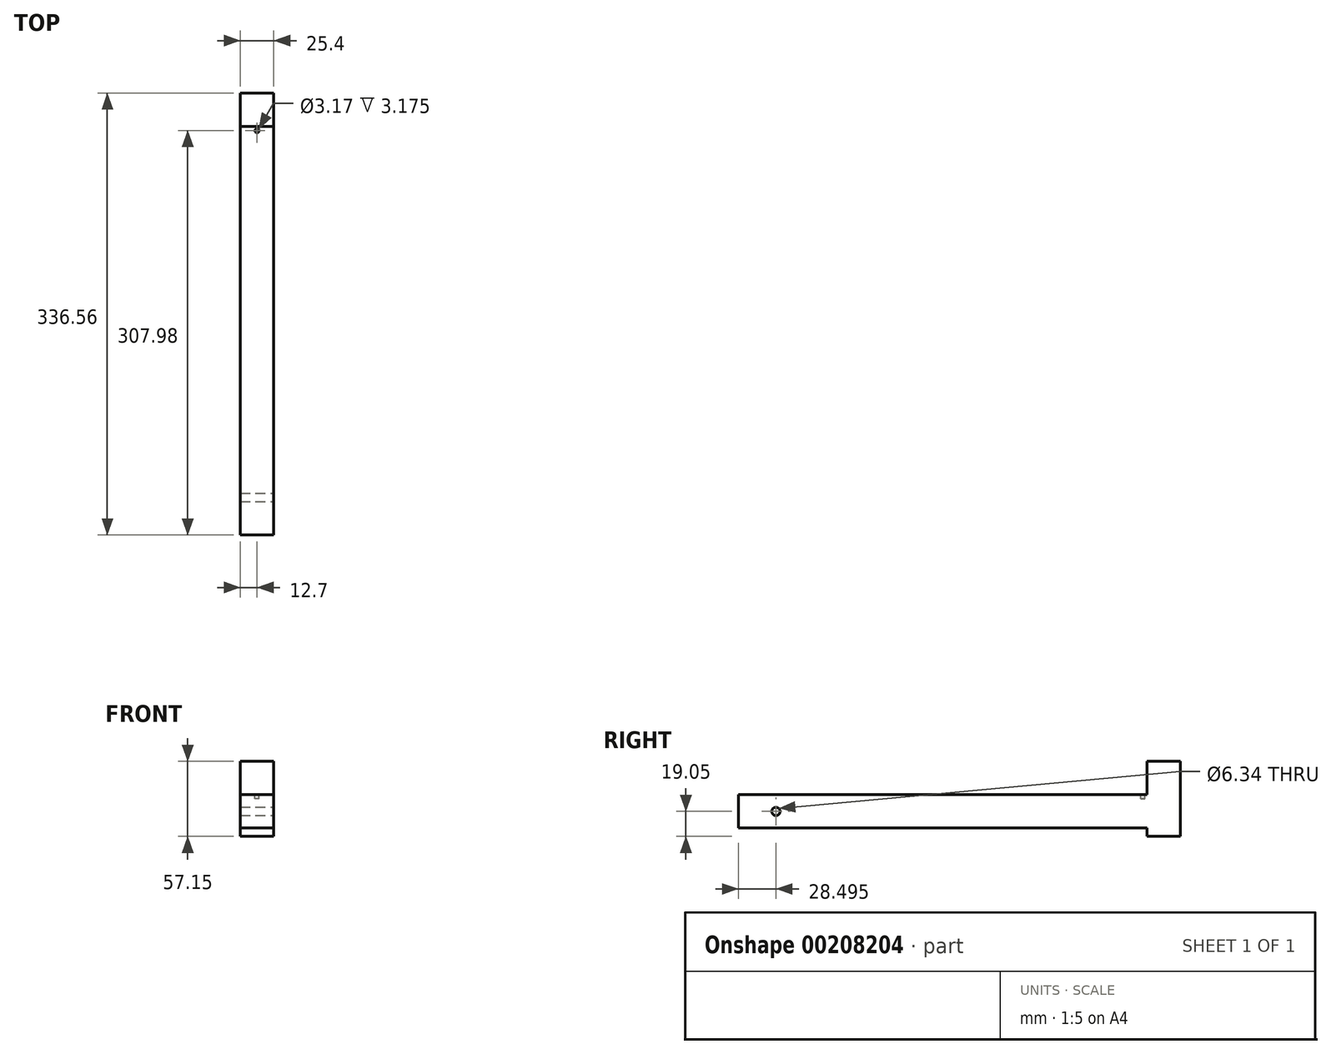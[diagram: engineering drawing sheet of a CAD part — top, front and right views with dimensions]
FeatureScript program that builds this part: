
annotation { "Feature Type Name" : "Feature", "Feature Type Description" : "" }
export const myFeature = defineFeature(function(context is Context, id is Id, definition is map)
    precondition{}
    {
        {
            var Q0;
            Q0=qCreatedBy(makeId("Right.planeOp"),FACE);
            var sketch = newSketch(context, id + "F0", { "sketchPlane" : qUnion([Q0])});
            skLineSegment(sketch, "E0.bottom", {"start": v(142.88, -12.7) * mm, "end": v(-168.28, -12.7) * mm});
            skLineSegment(sketch, "E0.top", {"start": v(142.88, 12.7) * mm, "end": v(-168.28, 12.7) * mm});
            skLineSegment(sketch, "E0.left", {"start": v(168.28, -12.7) * mm, "end": v(168.28, 12.7) * mm});
            skLineSegment(sketch, "E0.right", {"start": v(-168.28, -12.7) * mm, "end": v(-168.28, 12.7) * mm});
            skPoint(sketch, "E0.middle", {"position": v(0, 0) * mm});
            skLineSegment(sketch, "E1.top", {"start": v(168.28, 38.1) * mm, "end": v(142.88, 38.1) * mm});
            skLineSegment(sketch, "E1.left", {"start": v(168.28, 12.7) * mm, "end": v(168.28, 38.1) * mm});
            skLineSegment(sketch, "E1.right", {"start": v(142.88, 12.7) * mm, "end": v(142.88, 38.1) * mm});
            skLineSegment(sketch, "E2.top", {"start": v(168.28, -19.05) * mm, "end": v(142.88, -19.05) * mm});
            skLineSegment(sketch, "E2.left", {"start": v(168.28, -12.7) * mm, "end": v(168.28, -19.05) * mm});
            skLineSegment(sketch, "E2.right", {"start": v(142.88, -12.7) * mm, "end": v(142.88, -19.05) * mm});
            skSolve(sketch);
        }
        {
            var Q0;
            Q0 = qSketchRegion(id + "F0", true);
            extrude(context, id + "F1", {"entities" : qUnion([Q0]), "depth" : 25.4 * mm});
        }
        {
            var Q0;
            Q0=makeQuery(id+"F1.opExtrude","CAP_FACE",FACE,{"disambiguationData":[OSD([sQuery(id+"F0.wireOp",EDGE,"E0.bottom"),sQuery(id+"F0.wireOp",EDGE,"E0.top"),sQuery(id+"F0.wireOp",EDGE,"E0.left"),sQuery(id+"F0.wireOp",EDGE,"E0.right"),sQuery(id+"F0.wireOp",EDGE,"E1.top"),sQuery(id+"F0.wireOp",EDGE,"E1.left"),sQuery(id+"F0.wireOp",EDGE,"E1.right")])],"isStart":false});
            var sketch = newSketch(context, id + "F2", { "sketchPlane" : qUnion([Q0])});
            skLineSegment(sketch, "E3", {"start": v(-168.28, 0) * mm, "end": v(-142.88, 0) * mm, "construction": true});
            skLineSegment(sketch, "E4", {"start": v(-168.28, 0) * mm, "end": v(-136.53, 0) * mm, "construction": true});
            skPoint(sketch, "E4.endSnap0", {"position": v(-155.58, 0) * mm});
            skCircle(sketch, "E5", {"center": v(-139.79, 0) * mm, "radius": 3.17 * mm});
            skSolve(sketch);
        }
        {
            var Q0;
            Q0 = qSketchRegion(id + "F2", true);
            extrude(context, id + "F3", {"entities" : qUnion([Q0]), "operationType" : NewBodyOperationType.REMOVE, "endBound" : BoundingType.THROUGH_ALL, "oppositeDirection" : true, "depth" : 25.4 * mm});
        }
        {
            var Q0;
            Q0=makeQuery(id+"F1.opExtrude","SWEPT_FACE",FACE,{"disambiguationData":[OSD([sQuery(id+"F0.wireOp",EDGE,"E0.top")])]});
            var sketch = newSketch(context, id + "F4", { "sketchPlane" : qUnion([Q0])});
            skLineSegment(sketch, "E6", {"start": v(12.7, 142.88) * mm, "end": v(12.7, 136.53) * mm, "construction": true});
            skCircle(sketch, "E7", {"center": v(12.7, 139.7) * mm, "radius": 1.59 * mm});
            skSolve(sketch);
        }
        {
            var Q0;
            Q0 = qSketchRegion(id + "F4", true);
            extrude(context, id + "F5", {"entities" : qUnion([Q0]), "operationType" : NewBodyOperationType.REMOVE, "oppositeDirection" : true, "depth" : 3.17 * mm});
        }
    });
